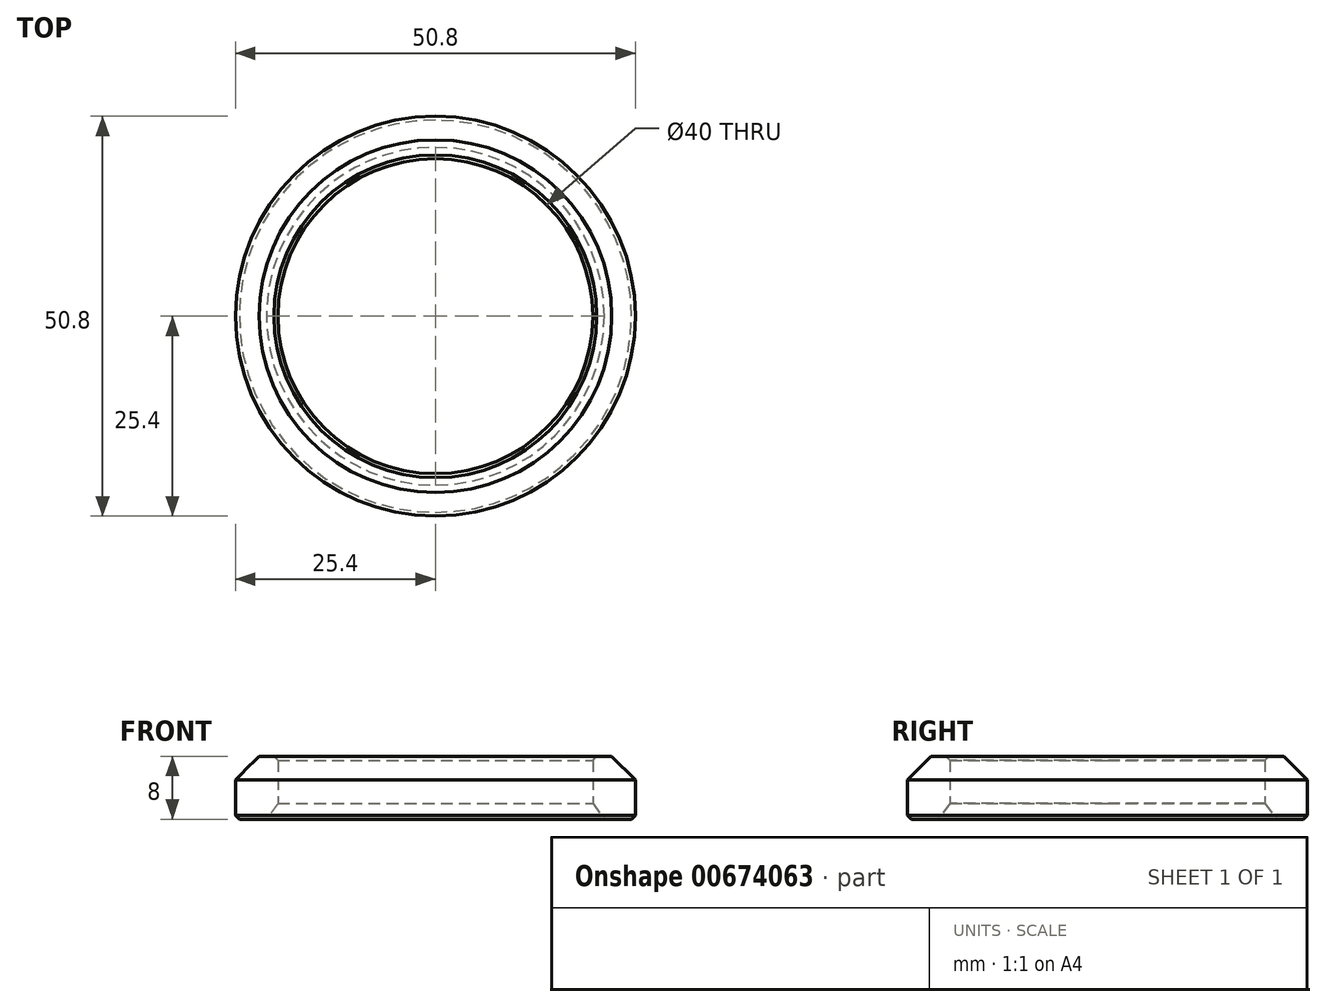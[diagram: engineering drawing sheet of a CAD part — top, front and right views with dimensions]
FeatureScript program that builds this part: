
annotation { "Feature Type Name" : "Feature", "Feature Type Description" : "" }
export const myFeature = defineFeature(function(context is Context, id is Id, definition is map)
    precondition{}
    {
        {
            var Q0;
            Q0=qCreatedBy(makeId("Right.planeOp"),FACE);
            var sketch = newSketch(context, id + "F0", { "sketchPlane" : qUnion([Q0])});
            skLineSegment(sketch, "E0", {"start": v(20, 0) * mm, "end": v(25.4, 0) * mm, "construction": true});
            skLineSegment(sketch, "E1", {"start": v(25.4, 0) * mm, "end": v(25.4, 8) * mm, "construction": true});
            skLineSegment(sketch, "E2", {"start": v(25.4, 8) * mm, "end": v(20, 8) * mm, "construction": true});
            skLineSegment(sketch, "E3", {"start": v(20, 8) * mm, "end": v(20, 0) * mm, "construction": true});
            skLineSegment(sketch, "E4", {"start": v(0, 0) * mm, "end": v(20, 0) * mm, "construction": true});
            skLineSegment(sketch, "E5", {"start": v(22.4, 8) * mm, "end": v(25.4, 5) * mm});
            skLineSegment(sketch, "E6", {"start": v(20, 8) * mm, "end": v(22.4, 8) * mm});
            skLineSegment(sketch, "E7", {"start": v(25.4, 5) * mm, "end": v(25.4, 0) * mm});
            skLineSegment(sketch, "E8", {"start": v(20, 2) * mm, "end": v(21.45, 0) * mm});
            skLineSegment(sketch, "E9", {"start": v(20, 8) * mm, "end": v(20, 2) * mm});
            skLineSegment(sketch, "E10", {"start": v(21.45, 0) * mm, "end": v(25.4, 0) * mm});
            skLineSegment(sketch, "E11", {"start": v(0, 0) * mm, "end": v(0, 40.06) * mm, "construction": true});
            skSolve(sketch);
        }
        {
            var Q0;
            Q0=makeQuery(id+"F0.imprint","IMPRINT",FACE,{"disambiguationData":[TD([[makeQuery(id+"F0.imprint","IMPRINT",EDGE,{"derivedFrom":sQuery(id+"F0.wireOp",EDGE,"E5")}),-1.0]])]});
            var Q1;
            Q1=sQuery(id+"F0.wireOp",EDGE,"E11");
            revolve(context, id + "F1", {"entities" : qUnion([Q0]), "axis" : qUnion([Q1]), "revolveType" : RevolveType.FULL});
        }
        {
            var Q0;
            Q0=makeQuery(id+"F1.opRevolve","SWEPT_EDGE",EDGE,{"disambiguationData":[OSD([sQuery(id+"F0.wireOp",EDGE,"E7"),sQuery(id+"F0.wireOp",EDGE,"E10")])]});
            chamfer(context, id + "F2", {"entities" : qUnion([Q0]), "width" : .5 * mm, "tangentPropagation" : true});
        }
        {
            var Q0;
            Q0=makeQuery(id+"F1.opRevolve","SWEPT_EDGE",EDGE,{"disambiguationData":[OSD([sQuery(id+"F0.wireOp",EDGE,"E6"),sQuery(id+"F0.wireOp",EDGE,"E9")])]});
            chamfer(context, id + "F3", {"entities" : qUnion([Q0]), "width" : .5 * mm, "tangentPropagation" : true});
        }
    });
